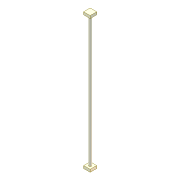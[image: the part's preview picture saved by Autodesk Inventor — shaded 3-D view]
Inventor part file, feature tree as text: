
AUTODESK INVENTOR PART (.ipt)
format: ipt  version: unknown  size: 168,448 bytes
history: native  units: mm
features: extrude x2, sketch x2, mirror x1
ambient origin geometry x8: Origin, YZ Plane, XZ Plane, XY Plane, X Axis, Y Axis, Z Axis, Center Point
feature tree (5):
  extrude  "Extrusion1"  Depth=10.0mm
  extrude  "Extrusion2"  Depth=104.0mm TaperAngle=0.0deg
  mirror  "Mirror1"
  sketch  "Sketch1"  dims[d0=4.0mm d1=10.0mm]
  sketch  "Sketch2"  dims[d2=4.0mm d3=0.0mm d4=104.0mm d5=0.0mm]
